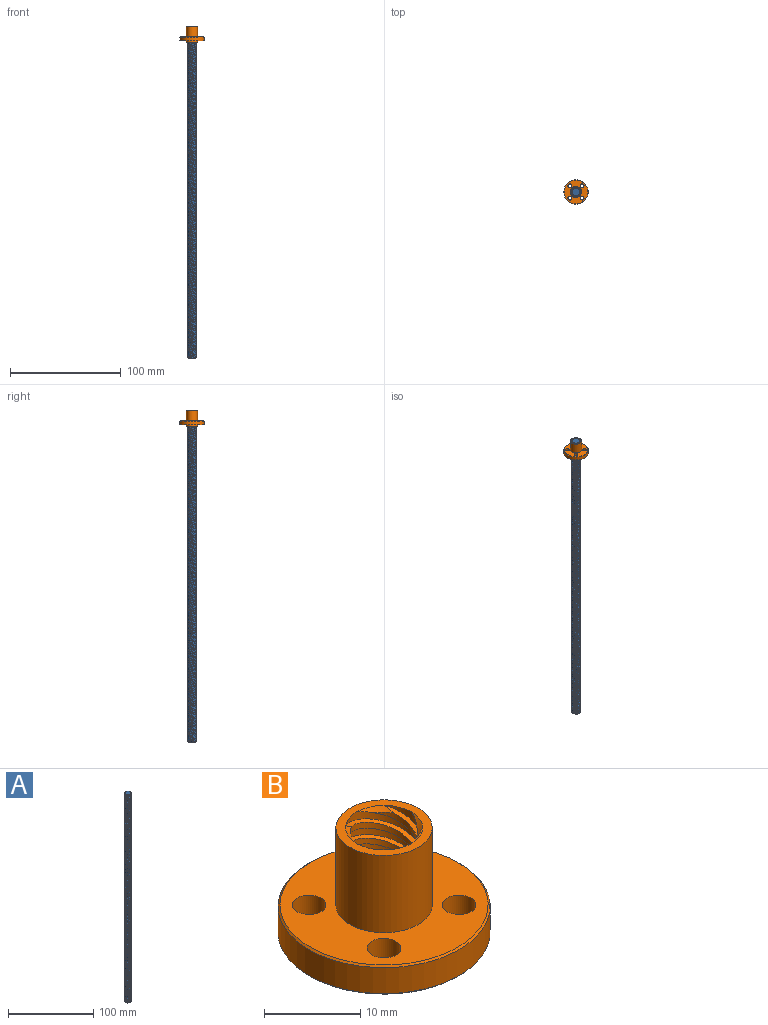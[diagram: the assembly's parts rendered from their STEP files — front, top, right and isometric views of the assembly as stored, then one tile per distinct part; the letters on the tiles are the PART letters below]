
ASSEMBLY  parts=2 mates=1
PART A: 26 faces, bbox 2094x2094x581.3 mm
  f0: cone r=4mm half-angle=45deg, axis (0,0,1), area 2.4mm2, adj f3,f18,f19,f23
  f1: cylinder r=4mm len=299mm, axis (0,0,-1), area 943.4mm2, adj f5,f6,f8,f9
  f2: cone r=3.5mm half-angle=45deg, axis (0,0,-1), area 2.3mm2, adj f3,f19,f20,f23
  f3: bspline ~301.13x8mm, area 482.1mm2, adj f0,f2,f4,f19
  f4: cylinder r=3.5mm len=300mm, axis (0,0,1), area 792.2mm2, adj f3,f5,f18,f20
  f5: bspline ~1051.52x581.26mm, area 480.4mm2, adj f1,f4,f6,f8
  f6: cone r=4mm half-angle=45deg, axis (0,0,1), area 2.4mm2, adj f1,f5,f9,f18
  f7: cylinder r=4mm len=299mm, axis (0,0,-1), area 943.4mm2, adj f11,f12,f14,f15
  f8: cone r=3.5mm half-angle=45deg, axis (0,0,-1), area 2.3mm2, adj f1,f5,f9,f20
  f9: bspline ~301.13x8mm, area 482.1mm2, adj f1,f6,f8,f10
  f10: cylinder r=3.5mm len=300mm, axis (0,0,1), area 792.2mm2, adj f9,f11,f18,f20
  f11: bspline ~1051.52x581.26mm, area 480.4mm2, adj f7,f10,f12,f14
  f12: cone r=4mm half-angle=45deg, axis (0,0,1), area 2.4mm2, adj f7,f11,f15,f18
  f13: cylinder r=4mm len=299mm, axis (0,0,-1), area 943.4mm2, adj f17,f22,f24,f25
  f14: cone r=3.5mm half-angle=45deg, axis (0,0,-1), area 2.3mm2, adj f7,f11,f15,f20
  f15: bspline ~301.13x8mm, area 482.1mm2, adj f7,f12,f14,f16
  f16: cylinder r=3.5mm len=300mm, axis (0,0,1), area 792.2mm2, adj f15,f17,f18,f20
  f17: bspline ~1051.52x581.26mm, area 480.4mm2, adj f13,f16,f24,f25
  f18: plane 7x7mm, normal (0,0,-1), area 38.5mm2, adj f0,f4,f6,f10,f12,f16,f21,f25
  f19: cylinder r=4mm len=299mm, axis (0,0,-1), area 943.4mm2, adj f0,f2,f3,f23
  f20: plane 7x7mm, normal (0,0,1), area 38.5mm2, adj f2,f4,f8,f10,f14,f16,f21,f24
  f21: cylinder r=3.5mm len=300mm, axis (0,0,1), area 792.2mm2, adj f18,f20,f22,f23
  f22: bspline ~301.13x8mm, area 482.1mm2, adj f13,f21,f24,f25
  f23: bspline ~1051.52x581.26mm, area 480.4mm2, adj f0,f2,f19,f21
  f24: cone r=3.5mm half-angle=45deg, axis (0,0,-1), area 2.3mm2, adj f13,f17,f20,f22
  f25: cone r=4mm half-angle=45deg, axis (0,0,1), area 2.4mm2, adj f13,f17,f18,f22
PART B: 37 faces, bbox 22x22x16.4 mm
  f0: cylinder r=1.75mm len=3.7mm, axis (0,0,-1), area 40.7mm2, adj f5,f6
  f1: cylinder r=1.75mm len=3.7mm, axis (0,0,-1), area 40.7mm2, adj f5,f6
  f2: cylinder r=1.75mm len=3.7mm, axis (0,0,-1), area 40.7mm2, adj f5,f6
  f3: cylinder r=1.75mm len=3.7mm, axis (0,0,-1), area 40.7mm2, adj f5,f6
  f4: cylinder r=11mm len=22mm, axis (0,0,-1), area 228.1mm2, adj f27,f28
  f5: plane 21.6x21.6mm, normal (0,0,1), area 249.4mm2, adj f0,f1,f2,f3,f9,f28
  f6: plane 21.6x21.6mm, normal (0,0,-1), area 249.4mm2, adj f0,f1,f2,f3,f8,f27
  f7: plane 10x10mm, normal (0,0,-1), area 28.3mm2, adj f8,f11,f15,f19,f23,f29,f30,f31
  f8: cylinder r=5mm len=10mm, axis (0,0,-1), area 47.1mm2, adj f6,f7
  f9: cylinder r=5mm len=10mm, axis (0,0,-1), area 307.9mm2, adj f5,f10
  f10: plane 10x10mm, normal (0,0,1), area 28.3mm2, adj f9,f11,f15,f19,f23,f33,f34,f35
  f11: cylinder r=4mm len=15mm, axis (0,0,-1), area 47.1mm2, adj f7,f10,f14,f16
  f12: bspline ~16.13x8mm, area 23.3mm2, adj f13,f23,f30,f36
  f13: cylinder r=3.5mm len=14mm, axis (0,0,1), area 28.2mm2, adj f12,f14,f30,f36
  f14: bspline ~16.4x9mm, area 23.3mm2, adj f11,f13,f30,f36
  f15: cylinder r=4mm len=15mm, axis (0,0,-1), area 47.1mm2, adj f7,f10,f18,f20
  f16: bspline ~16.13x8mm, area 23.3mm2, adj f11,f17,f29,f35
  f17: cylinder r=3.5mm len=14mm, axis (0,0,1), area 28.2mm2, adj f16,f18,f29,f35
  f18: bspline ~16.4x9mm, area 23.3mm2, adj f15,f17,f29,f35
  f19: cylinder r=4mm len=15mm, axis (0,0,-1), area 47.1mm2, adj f7,f10,f22,f25
  f20: bspline ~16.13x8mm, area 23.3mm2, adj f15,f21,f32,f34
  f21: cylinder r=3.5mm len=14mm, axis (0,0,1), area 28.2mm2, adj f20,f22,f32,f34
  f22: bspline ~16.4x9mm, area 23.3mm2, adj f19,f21,f32,f34
  f23: cylinder r=4mm len=15mm, axis (0,0,-1), area 47.1mm2, adj f7,f10,f12,f26
  f24: cylinder r=3.5mm len=14mm, axis (0,0,1), area 28.2mm2, adj f25,f26,f31,f33
  f25: bspline ~16.13x8mm, area 23.3mm2, adj f19,f24,f31,f33
  f26: bspline ~16.4x9mm, area 23.3mm2, adj f23,f24,f31,f33
  f27: cone r=11mm half-angle=45deg, axis (0,0,1), area 19.4mm2, adj f4,f6
  f28: cone r=10.8mm half-angle=45deg, axis (0,0,-1), area 19.4mm2, adj f4,f5
  f29: cone r=4mm half-angle=45deg, axis (0,0,-1), area 1.8mm2, adj f7,f16,f17,f18
  f30: cone r=4mm half-angle=45deg, axis (0,0,-1), area 1.8mm2, adj f7,f12,f13,f14
  f31: cone r=4mm half-angle=45deg, axis (0,0,-1), area 1.8mm2, adj f7,f24,f25,f26
  f32: cone r=4mm half-angle=45deg, axis (0,0,-1), area 1.8mm2, adj f7,f20,f21,f22
  f33: cone r=3.5mm half-angle=45deg, axis (0,0,1), area 1.8mm2, adj f10,f24,f25,f26
  f34: cone r=3.5mm half-angle=45deg, axis (0,0,1), area 1.8mm2, adj f10,f20,f21,f22
  f35: cone r=3.5mm half-angle=45deg, axis (0,0,1), area 1.8mm2, adj f10,f16,f17,f18
  f36: cone r=3.5mm half-angle=45deg, axis (0,0,1), area 1.8mm2, adj f10,f12,f13,f14
PLACE A t=(-73.14,20.65,-55.36)mm fixed
PLACE B t=(-73.14,20.65,223.14)mm
MATE cylindrical A.f0 <-> B.f4  axis (0,0,1) through (-73.14,20.65,244.64)mm
